# Revit family: Grille-Supply-Carnes-RTDB-Steel_Register
name_source: partatom
category: Duct Accessories
revit_build: Autodesk Revit Architecture 2013 (Build: 20120221_2030(x64)
units: mm (PartAtom-declared; Revit-internal decimal feet)

## types (10) — shared parameters
Assembly Code = D3040100
Catalog = http://www.carnes.com
Default Elevation = 0"
Description = Square and Rectangular Registers and Grilles
Flow = 0 CFM
Manufacturer = CARNES COMPANY
Model = RTDB
Product Page URL = http://www.carnes.com
Specification Sheet = http://www.carnes.com
Subcatagory = Air Distribution
Supply Connection = Diffuser Supply Connector
Supply Connector = Yes
URL = http://www.carnes.com
Unit = Metal - Carnes - Steel Galvanized

## per-type parameters (varying)
| type | Duct Height | Duct Width | Height | Inner Depth | Inner Width | Width |
| RTDB 8 x 4 | 6" | 2" | 4" | 1 1/2" | 5 1/2" | 8" |
| RTDB 10 x 4 | 8" | 2" | 4" | 1 1/2" | 7 1/2" | 10" |
| RTDB 8 x 6 | 6" | 4" | 6" | 3 1/2" | 5 1/2" | 8" |
| RTDB 10 x 6 | 8" | 4" | 6" | 3 1/2" | 7 1/2" | 10" |
| RTDB 12 x 6 | 10" | 4" | 6" | 3 1/2" | 9 1/2" | 12" |
| RTDB 16 x 6 | 14" | 4" | 6" | 3 1/2" | 13 1/2" | 16" |
| RTDB 20 x 6 | 18" | 4" | 6" | 3 1/2" | 17 1/2" | 20" |
| RTDB 24 x 6 | 22" | 4" | 6" | 3 1/2" | 21 1/2" | 24" |
| RTDB 24 x 8 | 22" | 6" | 8" | 5 1/2" | 21 1/2" | 24" |
| RTDB 24 x 10 | 22" | 8" | 10" | 7 1/2" | 21 1/2" | 24" |

## geometry (parser evidence)
native form markers: Blend x2, Sweep x10
no freeform markers — native parametric forms only
